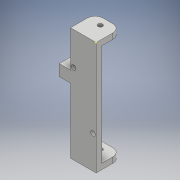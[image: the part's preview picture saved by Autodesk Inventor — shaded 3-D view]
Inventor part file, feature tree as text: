
AUTODESK INVENTOR PART (.ipt)
format: ipt  version: 2018 (Build 220112000, 112)  size: 355,840 bytes
history: native  units: mm
features: sketch x9, extrude x5, hole x3, fillet x2
ambient origin geometry x8: Origin, YZ Plane, XZ Plane, XY Plane, X Axis, Y Axis, Z Axis, Center Point
bodies: Solid1 (feature_tree)
feature tree (19):
  extrude  "Extrusion1"  Depth=100.0mm
  extrude  "Extrusion2"  Depth=5.0mm
  sketch  "Sketch3"  dims[d5=5.0mm d6=40.0mm d7=0.0mm]
  hole  "Hole1"  [1 undecoded]
  extrude  "Extrusion3"  Depth=2.0mm
  hole  "Hole2"  [1 undecoded]
  fillet  "Fillet1"  Radius=8.5mm
  extrude  "Extrusion4"  TaperAngle=90.0deg  [1 undecoded]
  extrude  "Extrusion5"  TaperAngle=180.0deg  [1 undecoded]
  hole  "Hole3"  [1 undecoded]
  fillet  "Fillet2"  Radius=3.5mm
  sketch  "Sketch1"  dims[d0=22.65mm d1=100.0mm]
  sketch  "Sketch2"  dims[d2=5.0mm d3=0.0mm d4=5.0mm]
  sketch  "Sketch4"  dims[d8=10.0mm]
  sketch  "Sketch5"  dims[d9=4.0mm d10=6.0mm d11=4.0mm d12=2.0mm d13=90.0deg d14=115.0mm d15=20.594885mm d16=23.0mm]
  sketch  "Sketch6"  dims[d17=102.75mm d18=0.0mm d19=1.175mm d20=8.5mm]
  sketch  "Sketch7"  dims[d21=21.0mm d22=90.0deg]
  sketch  "Sketch8"  dims[d23=8.5mm d24=180.0deg]
  sketch  "Sketch9"  dims[d25=21.0mm d26=4.0mm d27=6.0mm d28=4.0mm d29=2.0mm d30=90.0deg d31=115.0mm d32=20.594885mm d33=1.0mm d34=3.5mm d35=15.825mm d36=10.0mm d37=10.0mm d38=5.0mm d39=0.0mm d40=5.0mm d41=12.5mm d42=0.0mm d43=6.0mm d44=6.0mm d45=4.0mm d46=2.0mm d47=90.0deg d48=115.0mm d49=20.594885mm d50=7.0mm]
note: 5 required parameter values undecoded (feature->parameter linkage not recoverable at this tier; creation-order binding heuristic only, values carry confidence <= 0.55)
